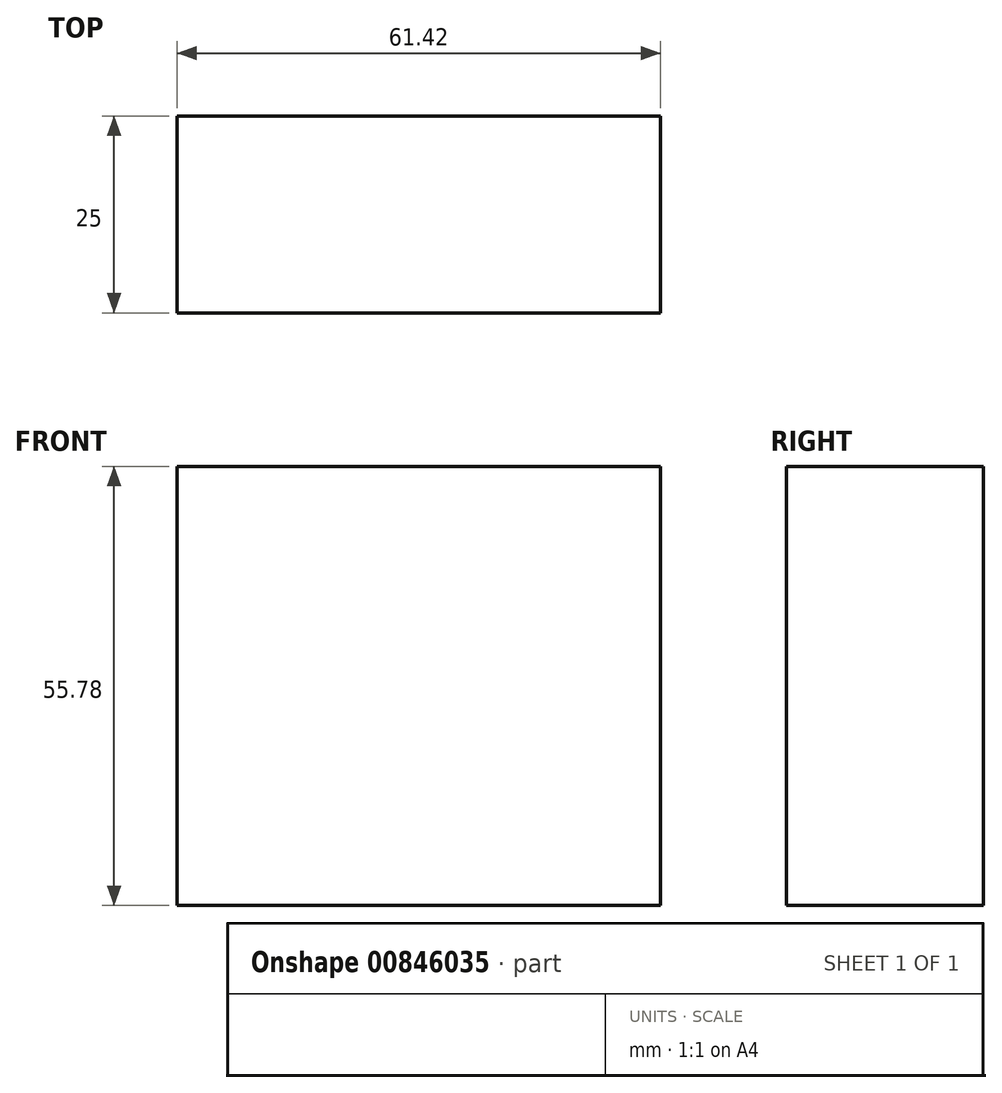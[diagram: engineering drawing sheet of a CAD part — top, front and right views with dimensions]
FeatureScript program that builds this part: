
annotation { "Feature Type Name" : "Feature", "Feature Type Description" : "" }
export const myFeature = defineFeature(function(context is Context, id is Id, definition is map)
    precondition{}
    {
        {
            var Q0;
            Q0=qCreatedBy(makeId("Front.planeOp"),FACE);
            var sketch = newSketch(context, id + "F0", { "sketchPlane" : qUnion([Q0])});
            skLineSegment(sketch, "E0.bottom", {"start": v(-129, 9.66) * mm, "end": v(-67.6, 9.66) * mm});
            skLineSegment(sketch, "E0.top", {"start": v(-129, 65.44) * mm, "end": v(-67.6, 65.44) * mm});
            skLineSegment(sketch, "E0.left", {"start": v(-129, 9.66) * mm, "end": v(-129, 65.44) * mm});
            skLineSegment(sketch, "E0.right", {"start": v(-67.6, 9.66) * mm, "end": v(-67.6, 65.44) * mm});
            skPoint(sketch, "E0.middle", {"position": v(-98.3, 37.55) * mm});
            skSolve(sketch);
        }
        {
            var Q0;
            Q0=makeQuery(id+"F0.imprint","IMPRINT",FACE,{"disambiguationData":[TD([[makeQuery(id+"F0.imprint","IMPRINT",EDGE,{"derivedFrom":sQuery(id+"F0.wireOp",EDGE,"E0.bottom")}),1.0]])]});
            extrude(context, id + "F1", {"entities" : qUnion([Q0]), "depth" : 25 * mm, "offsetDistance" : 25 * mm});
        }
    });
